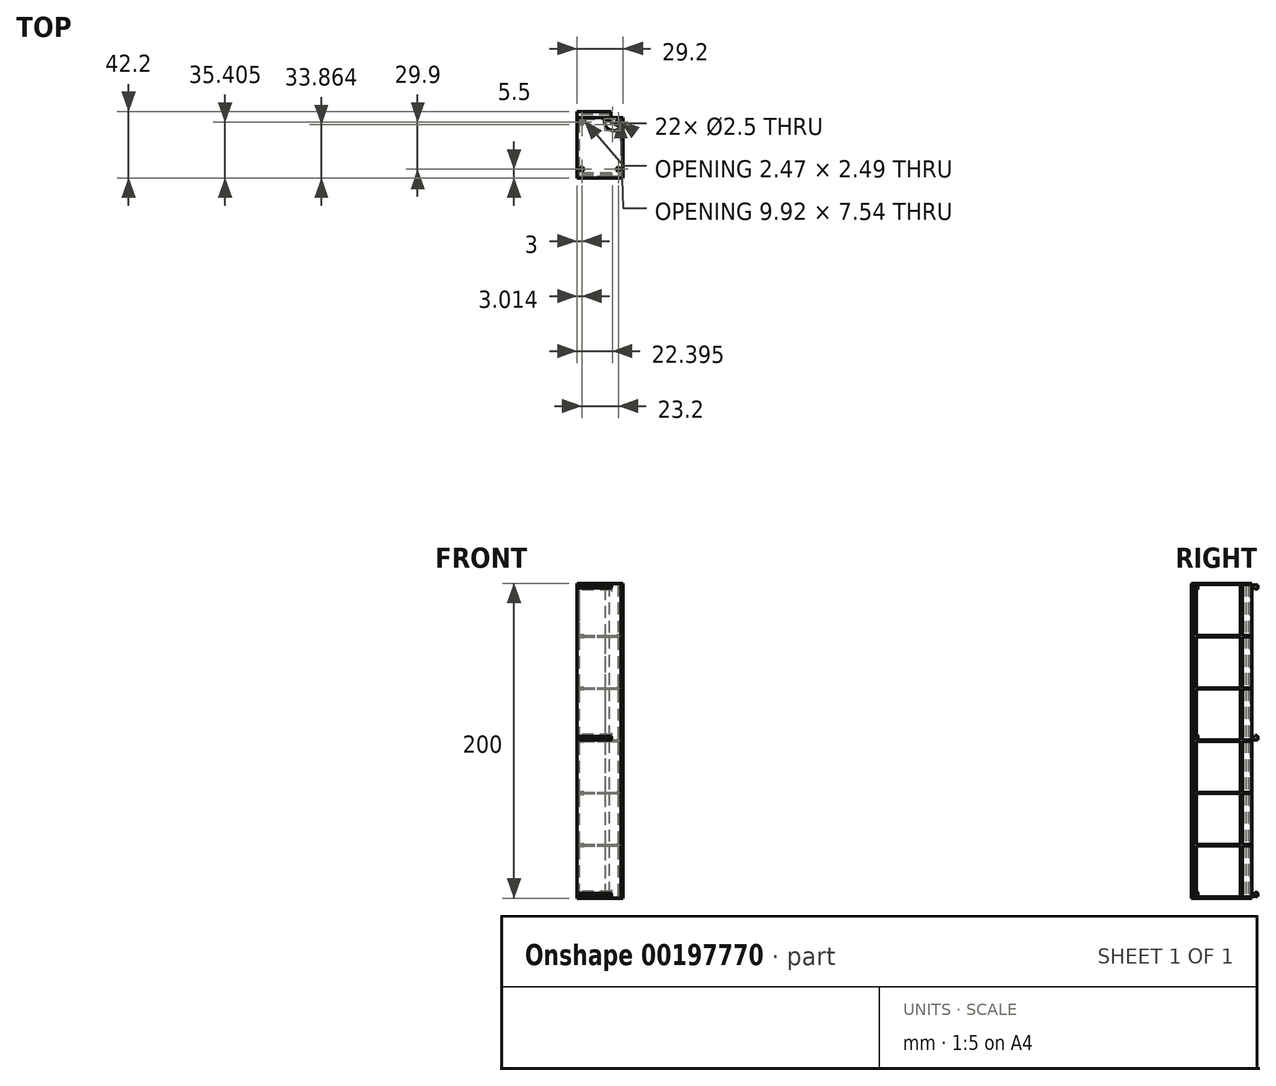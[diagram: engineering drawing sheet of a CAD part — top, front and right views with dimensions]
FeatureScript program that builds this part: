
annotation { "Feature Type Name" : "Feature", "Feature Type Description" : "" }
export const myFeature = defineFeature(function(context is Context, id is Id, definition is map)
    precondition{}
    {
        {
            var Q0;
            Q0=qCreatedBy(makeId("Top.planeOp"),FACE);
            var sketch = newSketch(context, id + "F0", { "sketchPlane" : qUnion([Q0])});
            skLineSegment(sketch, "E0.bottom", {"start": v(0, 0) * mm, "end": v(28, 0) * mm});
            skLineSegment(sketch, "E0.top", {"start": v(0, 38.4) * mm, "end": v(28, 38.4) * mm});
            skLineSegment(sketch, "E0.left", {"start": v(0, 0) * mm, "end": v(0, 38.4) * mm});
            skLineSegment(sketch, "E0.right", {"start": v(28, 0) * mm, "end": v(28, 38.4) * mm});
            skLineSegment(sketch, "E1.bottom", {"start": v(1.2, 37.2) * mm, "end": v(28, 37.2) * mm});
            skLineSegment(sketch, "E1.top", {"start": v(1.2, 1.2) * mm, "end": v(28, 1.2) * mm});
            skLineSegment(sketch, "E1.left", {"start": v(1.2, 37.2) * mm, "end": v(1.2, 1.2) * mm});
            skLineSegment(sketch, "E1.right", {"start": v(28, 37.2) * mm, "end": v(28, 1.2) * mm});
            skLineSegment(sketch, "E2", {"start": v(0.13, 0) * mm, "end": v(0, 0) * mm});
            skLineSegment(sketch, "E3", {"start": v(28, 1.2) * mm, "end": v(28, 3.2) * mm});
            skLineSegment(sketch, "E4", {"start": v(28, 3.2) * mm, "end": v(26, 1.2) * mm});
            skLineSegment(sketch, "E5", {"start": v(26, 1.2) * mm, "end": v(28, 1.2) * mm});
            skLineSegment(sketch, "E6", {"start": v(17.6, 37.2) * mm, "end": v(28, 31.2) * mm});
            skArc(sketch, "E7", {"start": v(17.6, 37.2) * mm, "mid": v(20.27, 30.81) * mm, "end": v(27.13, 31.7) * mm});
            skLineSegment(sketch, "E8", {"start": v(17.6, 37.2) * mm, "end": v(17.86, 37.63) * mm});
            skLineSegment(sketch, "E9", {"start": v(17.86, 37.63) * mm, "end": v(27.36, 32.15) * mm});
            skLineSegment(sketch, "E10", {"start": v(27.36, 32.15) * mm, "end": v(27.13, 31.7) * mm});
            skLineSegment(sketch, "E11.bottom", {"start": v(28, 31.2) * mm, "end": v(29.2, 31.2) * mm});
            skLineSegment(sketch, "E11.top", {"start": v(28, 32.4) * mm, "end": v(29.2, 32.4) * mm});
            skLineSegment(sketch, "E11.left", {"start": v(28, 31.2) * mm, "end": v(28, 32.4) * mm});
            skLineSegment(sketch, "E11.right", {"start": v(29.2, 31.2) * mm, "end": v(29.2, 32.4) * mm});
            skLineSegment(sketch, "E12.bottom", {"start": v(28, 3.2) * mm, "end": v(28, 3.2) * mm});
            skLineSegment(sketch, "E12.top", {"start": v(28, 1.2) * mm, "end": v(28, 1.2) * mm});
            skLineSegment(sketch, "E12.left", {"start": v(28, 3.2) * mm, "end": v(28, 1.2) * mm});
            skLineSegment(sketch, "E12.right", {"start": v(28, 3.2) * mm, "end": v(28, 1.2) * mm});
            skLineSegment(sketch, "E13.bottom", {"start": v(28, 3.2) * mm, "end": v(29.2, 3.2) * mm});
            skLineSegment(sketch, "E13.top", {"start": v(28, 2) * mm, "end": v(29.2, 2) * mm});
            skLineSegment(sketch, "E13.left", {"start": v(28, 3.2) * mm, "end": v(28, 2) * mm});
            skLineSegment(sketch, "E13.right", {"start": v(29.2, 3.2) * mm, "end": v(29.2, 2) * mm});
            skLineSegment(sketch, "E14", {"start": v(27.13, 31.7) * mm, "end": v(27.13, 37.2) * mm});
            skLineSegment(sketch, "E15", {"start": v(20.2, 37.2) * mm, "end": v(27.13, 33.2) * mm});
            skSolve(sketch);
        }
        {
            var Q0;
            {var subQ4=sQuery(id+"F0.wireOp",EDGE,"E0.bottom");Q0=makeQuery(id+"F0.imprint","IMPRINT",FACE,{"disambiguationData":[TD([[makeQuery(id+"F0.imprint","IMPRINT",EDGE,{"derivedFrom":subQ4}),1.0]])]});}
            var Q1;
            {var subQ0=sQuery(id+"F0.wireOp",EDGE,"E10");Q1=makeQuery(id+"F0.imprint","IMPRINT",FACE,{"disambiguationData":[TD([[makeQuery(id+"F0.imprint","IMPRINT",EDGE,{"derivedFrom":subQ0}),1.0]])]});}
            var Q2;
            Q2=makeQuery(id+"F0.imprint","IMPRINT",FACE,{"disambiguationData":[TD([[makeQuery(id+"F0.imprint","IMPRINT",EDGE,{"derivedFrom":sQuery(id+"F0.wireOp",EDGE,"E11.bottom")}),1.0]])]});
            var Q3;
            {var subQ0=sQuery(id+"F0.wireOp",EDGE,"E10");Q3=makeQuery(id+"F0.imprint","IMPRINT",FACE,{"disambiguationData":[TD([[makeQuery(id+"F0.imprint","IMPRINT",EDGE,{"derivedFrom":subQ0}),-1.0]])]});}
            var Q4;
            {var subQ0=sQuery(id+"F0.wireOp",EDGE,"E8");Q4=makeQuery(id+"F0.imprint","IMPRINT",FACE,{"disambiguationData":[TD([[makeQuery(id+"F0.imprint","IMPRINT",EDGE,{"derivedFrom":subQ0}),-1.0]])]});}
            var Q5;
            Q5=makeQuery(id+"F0.imprint","IMPRINT",FACE,{"disambiguationData":[TD([[makeQuery(id+"F0.imprint","IMPRINT",EDGE,{"derivedFrom":sQuery(id+"F0.wireOp",EDGE,"E4")}),1.0]])]});
            var Q6;
            Q6=makeQuery(id+"F0.imprint","IMPRINT",FACE,{"disambiguationData":[TD([[makeQuery(id+"F0.imprint","IMPRINT",EDGE,{"derivedFrom":sQuery(id+"F0.wireOp",EDGE,"E13.bottom")}),-1.0]])]});
            var Q7;
            {var subQ0=sQuery(id+"F0.wireOp",EDGE,"E15");Q7=makeQuery(id+"F0.imprint","IMPRINT",FACE,{"disambiguationData":[TD([[makeQuery(id+"F0.imprint","IMPRINT",EDGE,{"derivedFrom":subQ0}),-1.0]])]});}
            extrude(context, id + "F1", {"entities" : qUnion([Q0, Q1, Q2, Q3, Q4, Q5, Q6, Q7]), "depth" : 200 * mm});
        }
        {
            var Q0;
            Q0=qCreatedBy(makeId("Right.planeOp"),FACE);
            var sketch = newSketch(context, id + "F2", { "sketchPlane" : qUnion([Q0])});
            skLineSegment(sketch, "E16.bottom", {"start": v(0, 0) * mm, "end": v(38.4, 0) * mm});
            skLineSegment(sketch, "E16.top", {"start": v(0, 0.8) * mm, "end": v(38.4, 0.8) * mm});
            skLineSegment(sketch, "E16.left", {"start": v(0, 0) * mm, "end": v(0, 0.8) * mm});
            skLineSegment(sketch, "E16.right", {"start": v(38.4, 0) * mm, "end": v(38.4, 0.8) * mm});
            skLineSegment(sketch, "E17.0.1.0", {"start": v(0, 34) * mm, "end": v(38.4, 34) * mm});
            skLineSegment(sketch, "E17.0.1.1", {"start": v(0, 33.2) * mm, "end": v(38.4, 33.2) * mm});
            skLineSegment(sketch, "E17.0.1.2", {"start": v(0, 33.2) * mm, "end": v(0, 34) * mm});
            skLineSegment(sketch, "E17.0.1.3", {"start": v(38.4, 33.2) * mm, "end": v(38.4, 34) * mm});
            skLineSegment(sketch, "E17.0.2.0", {"start": v(0, 67.2) * mm, "end": v(38.4, 67.2) * mm});
            skLineSegment(sketch, "E17.0.2.1", {"start": v(0, 66.4) * mm, "end": v(38.4, 66.4) * mm});
            skLineSegment(sketch, "E17.0.2.2", {"start": v(0, 66.4) * mm, "end": v(0, 67.2) * mm});
            skLineSegment(sketch, "E17.0.2.3", {"start": v(38.4, 66.4) * mm, "end": v(38.4, 67.2) * mm});
            skLineSegment(sketch, "E17.0.3.0", {"start": v(0, 100.4) * mm, "end": v(38.4, 100.4) * mm});
            skLineSegment(sketch, "E17.0.3.1", {"start": v(0, 99.6) * mm, "end": v(38.4, 99.6) * mm});
            skLineSegment(sketch, "E17.0.3.2", {"start": v(0, 99.6) * mm, "end": v(0, 100.4) * mm});
            skLineSegment(sketch, "E17.0.3.3", {"start": v(38.4, 99.6) * mm, "end": v(38.4, 100.4) * mm});
            skLineSegment(sketch, "E17.0.4.0", {"start": v(0, 133.6) * mm, "end": v(38.4, 133.6) * mm});
            skLineSegment(sketch, "E17.0.4.1", {"start": v(0, 132.8) * mm, "end": v(38.4, 132.8) * mm});
            skLineSegment(sketch, "E17.0.4.2", {"start": v(0, 132.8) * mm, "end": v(0, 133.6) * mm});
            skLineSegment(sketch, "E17.0.4.3", {"start": v(38.4, 132.8) * mm, "end": v(38.4, 133.6) * mm});
            skLineSegment(sketch, "E17.0.5.0", {"start": v(0, 166.8) * mm, "end": v(38.4, 166.8) * mm});
            skLineSegment(sketch, "E17.0.5.1", {"start": v(0, 166) * mm, "end": v(38.4, 166) * mm});
            skLineSegment(sketch, "E17.0.5.2", {"start": v(0, 166) * mm, "end": v(0, 166.8) * mm});
            skLineSegment(sketch, "E17.0.5.3", {"start": v(38.4, 166) * mm, "end": v(38.4, 166.8) * mm});
            skLineSegment(sketch, "E17.direction1", {"start": v(0, 0) * mm, "end": v(25, 0) * mm, "construction": true});
            skLineSegment(sketch, "E17.direction2", {"start": v(0, 0) * mm, "end": v(0, 33.2) * mm, "construction": true});
            skLineSegment(sketch, "E18.0.0.6", {"start": v(0, 200) * mm, "end": v(38.4, 200) * mm});
            skLineSegment(sketch, "E18.3.0.6", {"start": v(0, 199.2) * mm, "end": v(38.4, 199.2) * mm});
            skLineSegment(sketch, "E18.6.0.6", {"start": v(0, 199.2) * mm, "end": v(0, 200) * mm});
            skLineSegment(sketch, "E18.9.0.6", {"start": v(38.4, 199.2) * mm, "end": v(38.4, 200) * mm});
            skSolve(sketch);
        }
        {
            var Q0;
            Q0=makeQuery(id+"F2.imprint","IMPRINT",FACE,{"disambiguationData":[TD([[makeQuery(id+"F2.imprint","IMPRINT",EDGE,{"derivedFrom":sQuery(id+"F2.wireOp",EDGE,"E16.bottom")}),1.0]])]});
            var Q1;
            Q1=makeQuery(id+"F2.imprint","IMPRINT",FACE,{"disambiguationData":[TD([[makeQuery(id+"F2.imprint","IMPRINT",EDGE,{"derivedFrom":sQuery(id+"F2.wireOp",EDGE,"E17.0.1.0")}),-1.0]])]});
            var Q2;
            Q2=makeQuery(id+"F2.imprint","IMPRINT",FACE,{"disambiguationData":[TD([[makeQuery(id+"F2.imprint","IMPRINT",EDGE,{"derivedFrom":sQuery(id+"F2.wireOp",EDGE,"E17.0.2.0")}),-1.0]])]});
            var Q3;
            Q3=makeQuery(id+"F2.imprint","IMPRINT",FACE,{"disambiguationData":[TD([[makeQuery(id+"F2.imprint","IMPRINT",EDGE,{"derivedFrom":sQuery(id+"F2.wireOp",EDGE,"E17.0.3.0")}),-1.0]])]});
            var Q4;
            Q4=makeQuery(id+"F2.imprint","IMPRINT",FACE,{"disambiguationData":[TD([[makeQuery(id+"F2.imprint","IMPRINT",EDGE,{"derivedFrom":sQuery(id+"F2.wireOp",EDGE,"E17.0.4.0")}),-1.0]])]});
            var Q5;
            Q5=makeQuery(id+"F2.imprint","IMPRINT",FACE,{"disambiguationData":[TD([[makeQuery(id+"F2.imprint","IMPRINT",EDGE,{"derivedFrom":sQuery(id+"F2.wireOp",EDGE,"E17.0.5.0")}),-1.0]])]});
            var Q6;
            Q6=makeQuery(id+"F2.imprint","IMPRINT",FACE,{"disambiguationData":[TD([[makeQuery(id+"F2.imprint","IMPRINT",EDGE,{"derivedFrom":sQuery(id+"F2.wireOp",EDGE,"E18.0.0.6")}),-1.0]])]});
            extrude(context, id + "F3", {"entities" : qUnion([Q0, Q1, Q2, Q3, Q4, Q5, Q6]), "operationType" : NewBodyOperationType.ADD, "depth" : 29.2 * mm});
        }
        {
            var Q0;
            {var subQ0=sQuery(id+"F0.wireOp",EDGE,"E7");Q0=makeQuery(id+"F0.imprint","IMPRINT",FACE,{"disambiguationData":[TD([[makeQuery(id+"F0.imprint","IMPRINT",EDGE,{"derivedFrom":subQ0}),1.0]])]});}
            var Q1;
            {var subQ2=sQuery(id+"F0.wireOp",EDGE,"E1.bottom");var subQ4=sQuery(id+"F0.wireOp",EDGE,"E9");var subQ5=makeQuery(id+"F0.imprint","INTERSECT",VERTEX,{"derivedFrom":[subQ2,subQ4]});Q1=makeQuery(id+"F0.imprint","IMPRINT",FACE,{"disambiguationData":[TD([[makeQuery(id+"F0.imprint","IMPRINT",EDGE,{"disambiguationData":[TD([[subQ5,-1.0]])],"derivedFrom":subQ4}),-1.0]])]});}
            var Q2;
            {var subQ0=sQuery(id+"F0.wireOp",EDGE,"E8");Q2=makeQuery(id+"F0.imprint","IMPRINT",FACE,{"disambiguationData":[TD([[makeQuery(id+"F0.imprint","IMPRINT",EDGE,{"derivedFrom":subQ0}),-1.0]])]});}
            var Q3;
            {var subQ0=sQuery(id+"F0.wireOp",EDGE,"E10");Q3=makeQuery(id+"F0.imprint","IMPRINT",FACE,{"disambiguationData":[TD([[makeQuery(id+"F0.imprint","IMPRINT",EDGE,{"derivedFrom":subQ0}),-1.0]])]});}
            extrude(context, id + "F4", {"entities" : qUnion([Q0, Q1, Q2, Q3]), "operationType" : NewBodyOperationType.REMOVE, "endBound" : BoundingType.THROUGH_ALL, "depth" : 25 * mm});
        }
        {
            var Q0;
            Q0=qCreatedBy(makeId("Right.planeOp"),FACE);
            var sketch = newSketch(context, id + "F5", { "sketchPlane" : qUnion([Q0])});
            skPoint(sketch, "E19", {"position": v(4.2, 0.8) * mm});
            skLineSegment(sketch, "E20.bottom", {"start": v(4.2, 0.8) * mm, "end": v(0, 0.8) * mm});
            skLineSegment(sketch, "E20.top", {"start": v(4.2, 3.05) * mm, "end": v(0, 3.05) * mm});
            skLineSegment(sketch, "E20.left", {"start": v(4.2, 0.8) * mm, "end": v(4.2, 3.05) * mm});
            skLineSegment(sketch, "E20.right", {"start": v(0, 0.8) * mm, "end": v(0, 3.05) * mm});
            skPoint(sketch, "E21", {"position": v(38.4, 1.05) * mm});
            skLineSegment(sketch, "E22.bottom", {"start": v(38.4, 1.05) * mm, "end": v(42.2, 1.05) * mm});
            skLineSegment(sketch, "E22.top", {"start": v(38.4, 2.8) * mm, "end": v(42.2, 2.8) * mm});
            skLineSegment(sketch, "E22.left", {"start": v(38.4, 1.05) * mm, "end": v(38.4, 2.8) * mm});
            skLineSegment(sketch, "E22.right", {"start": v(42.2, 1.05) * mm, "end": v(42.2, 2.8) * mm});
            skPoint(sketch, "E23", {"position": v(40.3, 2.8) * mm});
            skArc(sketch, "E24", {"start": v(42.2, 2.8) * mm, "mid": v(41.25, 3.75) * mm, "end": v(40.3, 2.8) * mm});
            skPoint(sketch, "E25", {"position": v(38.4, 198.95) * mm});
            skLineSegment(sketch, "E26.bottom", {"start": v(38.4, 198.95) * mm, "end": v(42.2, 198.95) * mm});
            skLineSegment(sketch, "E26.top", {"start": v(38.4, 197.2) * mm, "end": v(42.2, 197.2) * mm});
            skLineSegment(sketch, "E26.left", {"start": v(38.4, 198.95) * mm, "end": v(38.4, 197.2) * mm});
            skLineSegment(sketch, "E26.right", {"start": v(42.2, 198.95) * mm, "end": v(42.2, 197.2) * mm});
            skPoint(sketch, "E27", {"position": v(40.3, 197.2) * mm});
            skArc(sketch, "E28", {"start": v(40.3, 197.2) * mm, "mid": v(41.25, 196.25) * mm, "end": v(42.2, 197.2) * mm});
            skPoint(sketch, "E29", {"position": v(4.2, 199.2) * mm});
            skLineSegment(sketch, "E30.bottom", {"start": v(4.2, 199.2) * mm, "end": v(0, 199.2) * mm});
            skLineSegment(sketch, "E30.top", {"start": v(4.2, 196.95) * mm, "end": v(0, 196.95) * mm});
            skLineSegment(sketch, "E30.left", {"start": v(4.2, 199.2) * mm, "end": v(4.2, 196.95) * mm});
            skLineSegment(sketch, "E30.right", {"start": v(0, 199.2) * mm, "end": v(0, 196.95) * mm});
            skPoint(sketch, "E31", {"position": v(1.7, 197.2) * mm});
            skArc(sketch, "E32", {"start": v(1.7, 197.2) * mm, "mid": v(2.81, 195.7) * mm, "end": v(4.2, 196.95) * mm});
            skPoint(sketch, "E33", {"position": v(4.2, 100.4) * mm});
            skPoint(sketch, "E34", {"position": v(38.4, 100.65) * mm});
            skLineSegment(sketch, "E35.bottom", {"start": v(4.2, 100.4) * mm, "end": v(0, 100.4) * mm});
            skLineSegment(sketch, "E35.top", {"start": v(4.2, 102.65) * mm, "end": v(0, 102.65) * mm});
            skLineSegment(sketch, "E35.left", {"start": v(4.2, 100.4) * mm, "end": v(4.2, 102.65) * mm});
            skLineSegment(sketch, "E35.right", {"start": v(0, 100.4) * mm, "end": v(0, 102.65) * mm});
            skLineSegment(sketch, "E36.bottom", {"start": v(38.4, 100.65) * mm, "end": v(42.2, 100.65) * mm});
            skLineSegment(sketch, "E36.top", {"start": v(38.4, 102.4) * mm, "end": v(42.2, 102.4) * mm});
            skLineSegment(sketch, "E36.left", {"start": v(38.4, 100.65) * mm, "end": v(38.4, 102.4) * mm});
            skLineSegment(sketch, "E36.right", {"start": v(42.2, 100.65) * mm, "end": v(42.2, 102.4) * mm});
            skPoint(sketch, "E37", {"position": v(40.3, 102.4) * mm});
            skPoint(sketch, "E38", {"position": v(1.7, 102.4) * mm});
            skArc(sketch, "E39", {"start": v(4.2, 102.65) * mm, "mid": v(2.81, 103.9) * mm, "end": v(1.7, 102.4) * mm});
            skArc(sketch, "E40", {"start": v(42.2, 102.4) * mm, "mid": v(41.25, 103.35) * mm, "end": v(40.3, 102.4) * mm});
            skPoint(sketch, "E41", {"position": v(1.7, 3.05) * mm});
            skArc(sketch, "E42", {"start": v(4.2, 3.05) * mm, "mid": v(2.95, 4.3) * mm, "end": v(1.7, 3.05) * mm});
            skPoint(sketch, "E43.oppositeSnap0", {"position": v(2.81, 195.7) * mm});
            skLineSegment(sketch, "E43.bottom", {"start": v(2.94, 196.95) * mm, "end": v(0, 196.95) * mm});
            skLineSegment(sketch, "E43.top", {"start": v(2.94, 195.7) * mm, "end": v(0, 195.7) * mm});
            skLineSegment(sketch, "E43.left", {"start": v(2.94, 196.95) * mm, "end": v(2.94, 195.7) * mm});
            skLineSegment(sketch, "E43.right", {"start": v(0, 196.95) * mm, "end": v(0, 195.7) * mm});
            skPoint(sketch, "E44.oppositeSnap0", {"position": v(2.81, 103.9) * mm});
            skLineSegment(sketch, "E44.bottom", {"start": v(2.94, 102.65) * mm, "end": v(0, 102.65) * mm});
            skLineSegment(sketch, "E44.top", {"start": v(2.94, 103.9) * mm, "end": v(0, 103.9) * mm});
            skLineSegment(sketch, "E44.left", {"start": v(2.94, 102.65) * mm, "end": v(2.94, 103.9) * mm});
            skLineSegment(sketch, "E44.right", {"start": v(0, 102.65) * mm, "end": v(0, 103.9) * mm});
            skPoint(sketch, "E45.oppositeSnap0", {"position": v(2.95, 4.3) * mm});
            skLineSegment(sketch, "E45.bottom", {"start": v(2.95, 3.05) * mm, "end": v(0, 3.05) * mm});
            skLineSegment(sketch, "E45.top", {"start": v(2.95, 4.3) * mm, "end": v(0, 4.3) * mm});
            skLineSegment(sketch, "E45.left", {"start": v(2.95, 3.05) * mm, "end": v(2.95, 4.3) * mm});
            skLineSegment(sketch, "E45.right", {"start": v(0, 3.05) * mm, "end": v(0, 4.3) * mm});
            skSolve(sketch);
        }
        {
            var Q0;
            {var subQ0=sQuery(id+"F5.wireOp",EDGE,"E24");Q0=makeQuery(id+"F5.imprint","IMPRINT",FACE,{"disambiguationData":[TD([[makeQuery(id+"F5.imprint","IMPRINT",EDGE,{"derivedFrom":subQ0}),1.0]])]});}
            var Q1;
            Q1=makeQuery(id+"F5.imprint","IMPRINT",FACE,{"disambiguationData":[TD([[makeQuery(id+"F5.imprint","IMPRINT",EDGE,{"derivedFrom":sQuery(id+"F5.wireOp",EDGE,"E22.bottom")}),1.0]])]});
            var Q2;
            {var subQ0=sQuery(id+"F5.wireOp",EDGE,"E40");Q2=makeQuery(id+"F5.imprint","IMPRINT",FACE,{"disambiguationData":[TD([[makeQuery(id+"F5.imprint","IMPRINT",EDGE,{"derivedFrom":subQ0}),1.0]])]});}
            var Q3;
            Q3=makeQuery(id+"F5.imprint","IMPRINT",FACE,{"disambiguationData":[TD([[makeQuery(id+"F5.imprint","IMPRINT",EDGE,{"derivedFrom":sQuery(id+"F5.wireOp",EDGE,"E36.bottom")}),1.0]])]});
            var Q4;
            Q4=makeQuery(id+"F5.imprint","IMPRINT",FACE,{"disambiguationData":[TD([[makeQuery(id+"F5.imprint","IMPRINT",EDGE,{"derivedFrom":sQuery(id+"F5.wireOp",EDGE,"gY82O2s0-sYJy-ffMf-cmsV-ESsBruhGdGu2.bottom")}),-1.0]])]});
            var Q5;
            {var subQ0=sQuery(id+"F5.wireOp",EDGE,"uAfWt3q4-HwsG-Vt9b-ALQe-PVtKQTuhPL3T");Q5=makeQuery(id+"F5.imprint","IMPRINT",FACE,{"disambiguationData":[TD([[makeQuery(id+"F5.imprint","IMPRINT",EDGE,{"derivedFrom":subQ0}),1.0]])]});}
            var Q6;
            Q6=makeQuery(id+"F5.imprint","IMPRINT",FACE,{"disambiguationData":[TD([[makeQuery(id+"F5.imprint","IMPRINT",EDGE,{"derivedFrom":sQuery(id+"F5.wireOp",EDGE,"E26.bottom")}),-1.0]])]});
            var Q7;
            {var subQ0=sQuery(id+"F5.wireOp",EDGE,"E28");Q7=makeQuery(id+"F5.imprint","IMPRINT",FACE,{"disambiguationData":[TD([[makeQuery(id+"F5.imprint","IMPRINT",EDGE,{"derivedFrom":subQ0}),1.0]])]});}
            extrude(context, id + "F6", {"entities" : qUnion([Q0, Q1, Q2, Q3, Q4, Q5, Q6, Q7]), "operationType" : NewBodyOperationType.ADD, "depth" : 21.5 * mm});
        }
        {
            var Q0;
            Q0=makeQuery(id+"F5.imprint","IMPRINT",FACE,{"disambiguationData":[TD([[makeQuery(id+"F5.imprint","IMPRINT",EDGE,{"derivedFrom":sQuery(id+"F5.wireOp",EDGE,"E20.bottom")}),-1.0]])]});
            var Q1;
            {var subQ0=sQuery(id+"F5.wireOp",EDGE,"TJ2nz3Tg-qa8B-ndmI-YGek-TkeadyqaH0GQ");Q1=makeQuery(id+"F5.imprint","IMPRINT",FACE,{"disambiguationData":[TD([[makeQuery(id+"F5.imprint","IMPRINT",EDGE,{"derivedFrom":subQ0}),1.0]])]});}
            var Q2;
            Q2=makeQuery(id+"F5.imprint","IMPRINT",FACE,{"disambiguationData":[TD([[makeQuery(id+"F5.imprint","IMPRINT",EDGE,{"derivedFrom":sQuery(id+"F5.wireOp",EDGE,"E35.bottom")}),-1.0]])]});
            var Q3;
            {var subQ0=sQuery(id+"F5.wireOp",EDGE,"E39");Q3=makeQuery(id+"F5.imprint","IMPRINT",FACE,{"disambiguationData":[TD([[makeQuery(id+"F5.imprint","IMPRINT",EDGE,{"derivedFrom":subQ0}),1.0]])]});}
            var Q4;
            {var subQ0=sQuery(id+"F5.wireOp",EDGE,"E32");Q4=makeQuery(id+"F5.imprint","IMPRINT",FACE,{"disambiguationData":[TD([[makeQuery(id+"F5.imprint","IMPRINT",EDGE,{"derivedFrom":subQ0}),1.0]])]});}
            var Q5;
            Q5=makeQuery(id+"F5.imprint","IMPRINT",FACE,{"disambiguationData":[TD([[makeQuery(id+"F5.imprint","IMPRINT",EDGE,{"derivedFrom":sQuery(id+"F5.wireOp",EDGE,"E30.bottom")}),1.0]])]});
            var Q6;
            Q6=makeQuery(id+"F5.imprint","IMPRINT",FACE,{"disambiguationData":[TD([[makeQuery(id+"F5.imprint","IMPRINT",EDGE,{"derivedFrom":sQuery(id+"F5.wireOp",EDGE,"HvaKNjzZ-sT6a-075N-tYYH-bLPdwN5mXiem.bottom")}),1.0]])]});
            var Q7;
            {var subQ0=sQuery(id+"F5.wireOp",EDGE,"Ff060n06-jdxk-J9pJ-gkks-ZQV2I6IPtSoz");Q7=makeQuery(id+"F5.imprint","IMPRINT",FACE,{"disambiguationData":[TD([[makeQuery(id+"F5.imprint","IMPRINT",EDGE,{"derivedFrom":subQ0}),1.0]])]});}
            var Q8;
            {var subQ0=sQuery(id+"F5.wireOp",EDGE,"E42");Q8=makeQuery(id+"F5.imprint","IMPRINT",FACE,{"disambiguationData":[TD([[makeQuery(id+"F5.imprint","IMPRINT",EDGE,{"derivedFrom":subQ0}),1.0]])]});}
            extrude(context, id + "F7", {"entities" : qUnion([Q0, Q1, Q2, Q3, Q4, Q5, Q6, Q7, Q8]), "operationType" : NewBodyOperationType.REMOVE, "depth" : 22 * mm});
        }
        {
            var Q0;
            Q0=qCreatedBy(makeId("Top.planeOp"),FACE);
            var sketch = newSketch(context, id + "F8", { "sketchPlane" : qUnion([Q0])});
            skCircle(sketch, "E46", {"center": v(26.2, 35.4) * mm, "radius": 1.25 * mm});
            skCircle(sketch, "E47", {"center": v(3, 35.4) * mm, "radius": 1.25 * mm});
            skCircle(sketch, "E48", {"center": v(3, 5.5) * mm, "radius": 1.25 * mm});
            skCircle(sketch, "E49", {"center": v(26.2, 5.5) * mm, "radius": 1.25 * mm});
            skSolve(sketch);
        }
        {
            var Q0;
            Q0=makeQuery(id+"F8.imprint","IMPRINT",FACE,{"disambiguationData":[TD([[makeQuery(id+"F8.imprint","IMPRINT",EDGE,{"derivedFrom":sQuery(id+"F8.wireOp",EDGE,"E46")}),1.0]])]});
            var Q1;
            Q1=makeQuery(id+"F8.imprint","IMPRINT",FACE,{"disambiguationData":[TD([[makeQuery(id+"F8.imprint","IMPRINT",EDGE,{"derivedFrom":sQuery(id+"F8.wireOp",EDGE,"E47")}),1.0]])]});
            var Q2;
            Q2=makeQuery(id+"F8.imprint","IMPRINT",FACE,{"disambiguationData":[TD([[makeQuery(id+"F8.imprint","IMPRINT",EDGE,{"derivedFrom":sQuery(id+"F8.wireOp",EDGE,"E49")}),1.0]])]});
            var Q3;
            Q3=makeQuery(id+"F8.imprint","IMPRINT",FACE,{"disambiguationData":[TD([[makeQuery(id+"F8.imprint","IMPRINT",EDGE,{"derivedFrom":sQuery(id+"F8.wireOp",EDGE,"E48")}),1.0]])]});
            extrude(context, id + "F9", {"entities" : qUnion([Q0, Q1, Q2, Q3]), "operationType" : NewBodyOperationType.REMOVE, "endBound" : BoundingType.THROUGH_ALL, "depth" : 5 * mm});
        }
        {
            var Q0;
            {var subQ3=sQuery(id+"F5.wireOp",EDGE,"E45.top");Q0=makeQuery(id+"F5.imprint","IMPRINT",FACE,{"disambiguationData":[TD([[makeQuery(id+"F5.imprint","IMPRINT",EDGE,{"derivedFrom":subQ3}),1.0]])]});}
            var Q1;
            {var subQ5=sQuery(id+"F5.wireOp",EDGE,"E44.right");Q1=makeQuery(id+"F5.imprint","IMPRINT",FACE,{"disambiguationData":[TD([[makeQuery(id+"F5.imprint","IMPRINT",EDGE,{"derivedFrom":subQ5}),-1.0]])]});}
            var Q2;
            {var subQ5=sQuery(id+"F5.wireOp",EDGE,"E43.right");Q2=makeQuery(id+"F5.imprint","IMPRINT",FACE,{"disambiguationData":[TD([[makeQuery(id+"F5.imprint","IMPRINT",EDGE,{"derivedFrom":subQ5}),1.0]])]});}
            extrude(context, id + "F10", {"entities" : qUnion([Q0, Q1, Q2]), "operationType" : NewBodyOperationType.ADD, "depth" : 22 * mm});
        }
        {
            var Q0;
            Q0=makeQuery(id+"F3.boolean.opBoolean","INTERSECT",EDGE,{"derivedFrom":[makeQuery(id+"F1.opExtrude","SWEPT_FACE",FACE,{"disambiguationData":[OSD([sQuery(id+"F0.wireOp",EDGE,"E1.top")])]}),makeQuery(id+"F3.opExtrude","SWEPT_FACE",FACE,{"disambiguationData":[OSD([sQuery(id+"F2.wireOp",EDGE,"E17.0.1.0")])]})]});
            var Q1;
            Q1=makeQuery(id+"F3.boolean.opBoolean","INTERSECT",EDGE,{"derivedFrom":[makeQuery(id+"F1.opExtrude","SWEPT_FACE",FACE,{"disambiguationData":[OSD([sQuery(id+"F0.wireOp",EDGE,"E1.top")])]}),makeQuery(id+"F3.opExtrude","SWEPT_FACE",FACE,{"disambiguationData":[OSD([sQuery(id+"F2.wireOp",EDGE,"E17.0.1.1")])]})]});
            var Q2;
            Q2=makeQuery(id+"F10.boolean.opBoolean","INTERSECT",EDGE,{"derivedFrom":[makeQuery(id+"F3.boolean.opBoolean","SPLIT",FACE,{"disambiguationData":[TD([makeQuery(id+"F3.opExtrude","SWEPT_FACE",FACE,{"disambiguationData":[OSD([sQuery(id+"F2.wireOp",EDGE,"E16.top")])]})])],"derivedFrom":makeQuery(id+"F1.opExtrude","SWEPT_FACE",FACE,{"disambiguationData":[OSD([sQuery(id+"F0.wireOp",EDGE,"E1.top")])]})}),makeQuery(id+"F10.opExtrude","SWEPT_FACE",FACE,{"disambiguationData":[OSD([sQuery(id+"F5.wireOp",EDGE,"E45.top")])]})]});
            var Q3;
            Q3=makeQuery(id+"F3.boolean.opBoolean","INTERSECT",EDGE,{"derivedFrom":[makeQuery(id+"F1.opExtrude","SWEPT_FACE",FACE,{"disambiguationData":[OSD([sQuery(id+"F0.wireOp",EDGE,"E1.top")])]}),makeQuery(id+"F3.opExtrude","SWEPT_FACE",FACE,{"disambiguationData":[OSD([sQuery(id+"F2.wireOp",EDGE,"E17.0.2.1")])]})]});
            var Q4;
            Q4=makeQuery(id+"F3.boolean.opBoolean","INTERSECT",EDGE,{"derivedFrom":[makeQuery(id+"F1.opExtrude","SWEPT_FACE",FACE,{"disambiguationData":[OSD([sQuery(id+"F0.wireOp",EDGE,"E1.top")])]}),makeQuery(id+"F3.opExtrude","SWEPT_FACE",FACE,{"disambiguationData":[OSD([sQuery(id+"F2.wireOp",EDGE,"E17.0.2.0")])]})]});
            var Q5;
            Q5=makeQuery(id+"F3.boolean.opBoolean","INTERSECT",EDGE,{"derivedFrom":[makeQuery(id+"F1.opExtrude","SWEPT_FACE",FACE,{"disambiguationData":[OSD([sQuery(id+"F0.wireOp",EDGE,"E1.top")])]}),makeQuery(id+"F3.opExtrude","SWEPT_FACE",FACE,{"disambiguationData":[OSD([sQuery(id+"F2.wireOp",EDGE,"E17.0.3.1")])]})]});
            var Q6;
            Q6=makeQuery(id+"F10.boolean.opBoolean","INTERSECT",EDGE,{"derivedFrom":[makeQuery(id+"F3.boolean.opBoolean","SPLIT",FACE,{"disambiguationData":[TD([makeQuery(id+"F3.opExtrude","SWEPT_FACE",FACE,{"disambiguationData":[OSD([sQuery(id+"F2.wireOp",EDGE,"E17.0.3.0")])]})])],"derivedFrom":makeQuery(id+"F1.opExtrude","SWEPT_FACE",FACE,{"disambiguationData":[OSD([sQuery(id+"F0.wireOp",EDGE,"E1.top")])]})}),makeQuery(id+"F10.opExtrude","SWEPT_FACE",FACE,{"disambiguationData":[OSD([sQuery(id+"F5.wireOp",EDGE,"E44.top")])]})]});
            var Q7;
            Q7=makeQuery(id+"F3.boolean.opBoolean","INTERSECT",EDGE,{"derivedFrom":[makeQuery(id+"F1.opExtrude","SWEPT_FACE",FACE,{"disambiguationData":[OSD([sQuery(id+"F0.wireOp",EDGE,"E1.top")])]}),makeQuery(id+"F3.opExtrude","SWEPT_FACE",FACE,{"disambiguationData":[OSD([sQuery(id+"F2.wireOp",EDGE,"E17.0.4.1")])]})]});
            var Q8;
            Q8=makeQuery(id+"F3.boolean.opBoolean","INTERSECT",EDGE,{"derivedFrom":[makeQuery(id+"F1.opExtrude","SWEPT_FACE",FACE,{"disambiguationData":[OSD([sQuery(id+"F0.wireOp",EDGE,"E1.top")])]}),makeQuery(id+"F3.opExtrude","SWEPT_FACE",FACE,{"disambiguationData":[OSD([sQuery(id+"F2.wireOp",EDGE,"E17.0.4.0")])]})]});
            var Q9;
            Q9=makeQuery(id+"F3.boolean.opBoolean","INTERSECT",EDGE,{"derivedFrom":[makeQuery(id+"F1.opExtrude","SWEPT_FACE",FACE,{"disambiguationData":[OSD([sQuery(id+"F0.wireOp",EDGE,"E1.top")])]}),makeQuery(id+"F3.opExtrude","SWEPT_FACE",FACE,{"disambiguationData":[OSD([sQuery(id+"F2.wireOp",EDGE,"E17.0.5.1")])]})]});
            var Q10;
            Q10=makeQuery(id+"F3.boolean.opBoolean","INTERSECT",EDGE,{"derivedFrom":[makeQuery(id+"F1.opExtrude","SWEPT_FACE",FACE,{"disambiguationData":[OSD([sQuery(id+"F0.wireOp",EDGE,"E1.top")])]}),makeQuery(id+"F3.opExtrude","SWEPT_FACE",FACE,{"disambiguationData":[OSD([sQuery(id+"F2.wireOp",EDGE,"E17.0.5.0")])]})]});
            var Q11;
            Q11=makeQuery(id+"F10.boolean.opBoolean","INTERSECT",EDGE,{"derivedFrom":[makeQuery(id+"F3.boolean.opBoolean","SPLIT",FACE,{"disambiguationData":[TD([makeQuery(id+"F3.opExtrude","SWEPT_FACE",FACE,{"disambiguationData":[OSD([sQuery(id+"F2.wireOp",EDGE,"E17.0.5.0")])]})])],"derivedFrom":makeQuery(id+"F1.opExtrude","SWEPT_FACE",FACE,{"disambiguationData":[OSD([sQuery(id+"F0.wireOp",EDGE,"E1.top")])]})}),makeQuery(id+"F10.opExtrude","SWEPT_FACE",FACE,{"disambiguationData":[OSD([sQuery(id+"F5.wireOp",EDGE,"E43.top")])]})]});
            var Q12;
            {var subQ0=sQuery(id+"F0.wireOp",EDGE,"E1.bottom");Q12=makeQuery(id+"F3.boolean.opBoolean","INTERSECT",EDGE,{"derivedFrom":[makeQuery(id+"F1.opExtrude","SWEPT_FACE",FACE,{"disambiguationData":[OSD([subQ0]),TDD([makeQuery(id+"F0.imprint","IMPRINT",EDGE,{"disambiguationData":[TD([[makeQuery(id+"F0.imprint","INTERSECT",VERTEX,{"derivedFrom":[subQ0,sQuery(id+"F0.wireOp",EDGE,"E1.left")]}),-1.0]])],"derivedFrom":subQ0}),makeQuery(id+"F0.imprint","IMPRINT",EDGE,{"disambiguationData":[TD([[makeQuery(id+"F0.imprint","INTERSECT",VERTEX,{"derivedFrom":[subQ0,sQuery(id+"F0.wireOp",EDGE,"E9")]}),1.0]])],"derivedFrom":subQ0})])]}),makeQuery(id+"F3.opExtrude","SWEPT_FACE",FACE,{"disambiguationData":[OSD([sQuery(id+"F2.wireOp",EDGE,"E18.3.0.6")])]})]});}
            var Q13;
            {var subQ0=sQuery(id+"F0.wireOp",EDGE,"E1.bottom");Q13=makeQuery(id+"F3.boolean.opBoolean","INTERSECT",EDGE,{"derivedFrom":[makeQuery(id+"F1.opExtrude","SWEPT_FACE",FACE,{"disambiguationData":[OSD([subQ0]),TDD([makeQuery(id+"F0.imprint","IMPRINT",EDGE,{"disambiguationData":[TD([[makeQuery(id+"F0.imprint","INTERSECT",VERTEX,{"derivedFrom":[subQ0,sQuery(id+"F0.wireOp",EDGE,"E1.left")]}),-1.0]])],"derivedFrom":subQ0}),makeQuery(id+"F0.imprint","IMPRINT",EDGE,{"disambiguationData":[TD([[makeQuery(id+"F0.imprint","INTERSECT",VERTEX,{"derivedFrom":[subQ0,sQuery(id+"F0.wireOp",EDGE,"E9")]}),1.0]])],"derivedFrom":subQ0})])]}),makeQuery(id+"F3.opExtrude","SWEPT_FACE",FACE,{"disambiguationData":[OSD([sQuery(id+"F2.wireOp",EDGE,"E17.0.5.0")])]})]});}
            var Q14;
            {var subQ0=sQuery(id+"F0.wireOp",EDGE,"E1.bottom");Q14=makeQuery(id+"F3.boolean.opBoolean","INTERSECT",EDGE,{"derivedFrom":[makeQuery(id+"F1.opExtrude","SWEPT_FACE",FACE,{"disambiguationData":[OSD([subQ0]),TDD([makeQuery(id+"F0.imprint","IMPRINT",EDGE,{"disambiguationData":[TD([[makeQuery(id+"F0.imprint","INTERSECT",VERTEX,{"derivedFrom":[subQ0,sQuery(id+"F0.wireOp",EDGE,"E1.left")]}),-1.0]])],"derivedFrom":subQ0}),makeQuery(id+"F0.imprint","IMPRINT",EDGE,{"disambiguationData":[TD([[makeQuery(id+"F0.imprint","INTERSECT",VERTEX,{"derivedFrom":[subQ0,sQuery(id+"F0.wireOp",EDGE,"E9")]}),1.0]])],"derivedFrom":subQ0})])]}),makeQuery(id+"F3.opExtrude","SWEPT_FACE",FACE,{"disambiguationData":[OSD([sQuery(id+"F2.wireOp",EDGE,"E17.0.5.1")])]})]});}
            var Q15;
            {var subQ0=sQuery(id+"F0.wireOp",EDGE,"E1.bottom");Q15=makeQuery(id+"F3.boolean.opBoolean","INTERSECT",EDGE,{"derivedFrom":[makeQuery(id+"F1.opExtrude","SWEPT_FACE",FACE,{"disambiguationData":[OSD([subQ0]),TDD([makeQuery(id+"F0.imprint","IMPRINT",EDGE,{"disambiguationData":[TD([[makeQuery(id+"F0.imprint","INTERSECT",VERTEX,{"derivedFrom":[subQ0,sQuery(id+"F0.wireOp",EDGE,"E1.left")]}),-1.0]])],"derivedFrom":subQ0}),makeQuery(id+"F0.imprint","IMPRINT",EDGE,{"disambiguationData":[TD([[makeQuery(id+"F0.imprint","INTERSECT",VERTEX,{"derivedFrom":[subQ0,sQuery(id+"F0.wireOp",EDGE,"E9")]}),1.0]])],"derivedFrom":subQ0})])]}),makeQuery(id+"F3.opExtrude","SWEPT_FACE",FACE,{"disambiguationData":[OSD([sQuery(id+"F2.wireOp",EDGE,"E17.0.4.0")])]})]});}
            var Q16;
            {var subQ0=sQuery(id+"F0.wireOp",EDGE,"E1.bottom");Q16=makeQuery(id+"F3.boolean.opBoolean","INTERSECT",EDGE,{"derivedFrom":[makeQuery(id+"F1.opExtrude","SWEPT_FACE",FACE,{"disambiguationData":[OSD([subQ0]),TDD([makeQuery(id+"F0.imprint","IMPRINT",EDGE,{"disambiguationData":[TD([[makeQuery(id+"F0.imprint","INTERSECT",VERTEX,{"derivedFrom":[subQ0,sQuery(id+"F0.wireOp",EDGE,"E1.left")]}),-1.0]])],"derivedFrom":subQ0}),makeQuery(id+"F0.imprint","IMPRINT",EDGE,{"disambiguationData":[TD([[makeQuery(id+"F0.imprint","INTERSECT",VERTEX,{"derivedFrom":[subQ0,sQuery(id+"F0.wireOp",EDGE,"E9")]}),1.0]])],"derivedFrom":subQ0})])]}),makeQuery(id+"F3.opExtrude","SWEPT_FACE",FACE,{"disambiguationData":[OSD([sQuery(id+"F2.wireOp",EDGE,"E17.0.4.1")])]})]});}
            var Q17;
            {var subQ0=sQuery(id+"F0.wireOp",EDGE,"E1.bottom");Q17=makeQuery(id+"F3.boolean.opBoolean","INTERSECT",EDGE,{"derivedFrom":[makeQuery(id+"F1.opExtrude","SWEPT_FACE",FACE,{"disambiguationData":[OSD([subQ0]),TDD([makeQuery(id+"F0.imprint","IMPRINT",EDGE,{"disambiguationData":[TD([[makeQuery(id+"F0.imprint","INTERSECT",VERTEX,{"derivedFrom":[subQ0,sQuery(id+"F0.wireOp",EDGE,"E1.left")]}),-1.0]])],"derivedFrom":subQ0}),makeQuery(id+"F0.imprint","IMPRINT",EDGE,{"disambiguationData":[TD([[makeQuery(id+"F0.imprint","INTERSECT",VERTEX,{"derivedFrom":[subQ0,sQuery(id+"F0.wireOp",EDGE,"E9")]}),1.0]])],"derivedFrom":subQ0})])]}),makeQuery(id+"F3.opExtrude","SWEPT_FACE",FACE,{"disambiguationData":[OSD([sQuery(id+"F2.wireOp",EDGE,"E17.0.3.0")])]})]});}
            var Q18;
            {var subQ0=sQuery(id+"F0.wireOp",EDGE,"E1.bottom");Q18=makeQuery(id+"F3.boolean.opBoolean","INTERSECT",EDGE,{"derivedFrom":[makeQuery(id+"F1.opExtrude","SWEPT_FACE",FACE,{"disambiguationData":[OSD([subQ0]),TDD([makeQuery(id+"F0.imprint","IMPRINT",EDGE,{"disambiguationData":[TD([[makeQuery(id+"F0.imprint","INTERSECT",VERTEX,{"derivedFrom":[subQ0,sQuery(id+"F0.wireOp",EDGE,"E1.left")]}),-1.0]])],"derivedFrom":subQ0}),makeQuery(id+"F0.imprint","IMPRINT",EDGE,{"disambiguationData":[TD([[makeQuery(id+"F0.imprint","INTERSECT",VERTEX,{"derivedFrom":[subQ0,sQuery(id+"F0.wireOp",EDGE,"E9")]}),1.0]])],"derivedFrom":subQ0})])]}),makeQuery(id+"F3.opExtrude","SWEPT_FACE",FACE,{"disambiguationData":[OSD([sQuery(id+"F2.wireOp",EDGE,"E17.0.3.1")])]})]});}
            var Q19;
            {var subQ0=sQuery(id+"F0.wireOp",EDGE,"E1.bottom");Q19=makeQuery(id+"F3.boolean.opBoolean","INTERSECT",EDGE,{"derivedFrom":[makeQuery(id+"F1.opExtrude","SWEPT_FACE",FACE,{"disambiguationData":[OSD([subQ0]),TDD([makeQuery(id+"F0.imprint","IMPRINT",EDGE,{"disambiguationData":[TD([[makeQuery(id+"F0.imprint","INTERSECT",VERTEX,{"derivedFrom":[subQ0,sQuery(id+"F0.wireOp",EDGE,"E1.left")]}),-1.0]])],"derivedFrom":subQ0}),makeQuery(id+"F0.imprint","IMPRINT",EDGE,{"disambiguationData":[TD([[makeQuery(id+"F0.imprint","INTERSECT",VERTEX,{"derivedFrom":[subQ0,sQuery(id+"F0.wireOp",EDGE,"E9")]}),1.0]])],"derivedFrom":subQ0})])]}),makeQuery(id+"F3.opExtrude","SWEPT_FACE",FACE,{"disambiguationData":[OSD([sQuery(id+"F2.wireOp",EDGE,"E17.0.2.0")])]})]});}
            var Q20;
            {var subQ0=sQuery(id+"F0.wireOp",EDGE,"E1.bottom");Q20=makeQuery(id+"F3.boolean.opBoolean","INTERSECT",EDGE,{"derivedFrom":[makeQuery(id+"F1.opExtrude","SWEPT_FACE",FACE,{"disambiguationData":[OSD([subQ0]),TDD([makeQuery(id+"F0.imprint","IMPRINT",EDGE,{"disambiguationData":[TD([[makeQuery(id+"F0.imprint","INTERSECT",VERTEX,{"derivedFrom":[subQ0,sQuery(id+"F0.wireOp",EDGE,"E1.left")]}),-1.0]])],"derivedFrom":subQ0}),makeQuery(id+"F0.imprint","IMPRINT",EDGE,{"disambiguationData":[TD([[makeQuery(id+"F0.imprint","INTERSECT",VERTEX,{"derivedFrom":[subQ0,sQuery(id+"F0.wireOp",EDGE,"E9")]}),1.0]])],"derivedFrom":subQ0})])]}),makeQuery(id+"F3.opExtrude","SWEPT_FACE",FACE,{"disambiguationData":[OSD([sQuery(id+"F2.wireOp",EDGE,"E17.0.2.1")])]})]});}
            var Q21;
            {var subQ0=sQuery(id+"F0.wireOp",EDGE,"E1.bottom");Q21=makeQuery(id+"F3.boolean.opBoolean","INTERSECT",EDGE,{"derivedFrom":[makeQuery(id+"F1.opExtrude","SWEPT_FACE",FACE,{"disambiguationData":[OSD([subQ0]),TDD([makeQuery(id+"F0.imprint","IMPRINT",EDGE,{"disambiguationData":[TD([[makeQuery(id+"F0.imprint","INTERSECT",VERTEX,{"derivedFrom":[subQ0,sQuery(id+"F0.wireOp",EDGE,"E1.left")]}),-1.0]])],"derivedFrom":subQ0}),makeQuery(id+"F0.imprint","IMPRINT",EDGE,{"disambiguationData":[TD([[makeQuery(id+"F0.imprint","INTERSECT",VERTEX,{"derivedFrom":[subQ0,sQuery(id+"F0.wireOp",EDGE,"E9")]}),1.0]])],"derivedFrom":subQ0})])]}),makeQuery(id+"F3.opExtrude","SWEPT_FACE",FACE,{"disambiguationData":[OSD([sQuery(id+"F2.wireOp",EDGE,"E17.0.1.0")])]})]});}
            var Q22;
            {var subQ0=sQuery(id+"F0.wireOp",EDGE,"E1.bottom");Q22=makeQuery(id+"F3.boolean.opBoolean","INTERSECT",EDGE,{"derivedFrom":[makeQuery(id+"F1.opExtrude","SWEPT_FACE",FACE,{"disambiguationData":[OSD([subQ0]),TDD([makeQuery(id+"F0.imprint","IMPRINT",EDGE,{"disambiguationData":[TD([[makeQuery(id+"F0.imprint","INTERSECT",VERTEX,{"derivedFrom":[subQ0,sQuery(id+"F0.wireOp",EDGE,"E1.left")]}),-1.0]])],"derivedFrom":subQ0}),makeQuery(id+"F0.imprint","IMPRINT",EDGE,{"disambiguationData":[TD([[makeQuery(id+"F0.imprint","INTERSECT",VERTEX,{"derivedFrom":[subQ0,sQuery(id+"F0.wireOp",EDGE,"E9")]}),1.0]])],"derivedFrom":subQ0})])]}),makeQuery(id+"F3.opExtrude","SWEPT_FACE",FACE,{"disambiguationData":[OSD([sQuery(id+"F2.wireOp",EDGE,"E17.0.1.1")])]})]});}
            var Q23;
            {var subQ0=sQuery(id+"F0.wireOp",EDGE,"E1.bottom");Q23=makeQuery(id+"F3.boolean.opBoolean","INTERSECT",EDGE,{"derivedFrom":[makeQuery(id+"F1.opExtrude","SWEPT_FACE",FACE,{"disambiguationData":[OSD([subQ0]),TDD([makeQuery(id+"F0.imprint","IMPRINT",EDGE,{"disambiguationData":[TD([[makeQuery(id+"F0.imprint","INTERSECT",VERTEX,{"derivedFrom":[subQ0,sQuery(id+"F0.wireOp",EDGE,"E1.left")]}),-1.0]])],"derivedFrom":subQ0}),makeQuery(id+"F0.imprint","IMPRINT",EDGE,{"disambiguationData":[TD([[makeQuery(id+"F0.imprint","INTERSECT",VERTEX,{"derivedFrom":[subQ0,sQuery(id+"F0.wireOp",EDGE,"E9")]}),1.0]])],"derivedFrom":subQ0})])]}),makeQuery(id+"F3.opExtrude","SWEPT_FACE",FACE,{"disambiguationData":[OSD([sQuery(id+"F2.wireOp",EDGE,"E16.top")])]})]});}
            fillet(context, id + "F11", {"entities" : qUnion([Q0, Q1, Q2, Q3, Q4, Q5, Q6, Q7, Q8, Q9, Q10, Q11, Q12, Q13, Q14, Q15, Q16, Q17, Q18, Q19, Q20, Q21, Q22, Q23]), "radius" : 1 * mm, "tangentPropagation" : true, "allowEdgeOverflow" : false});
        }
    });
